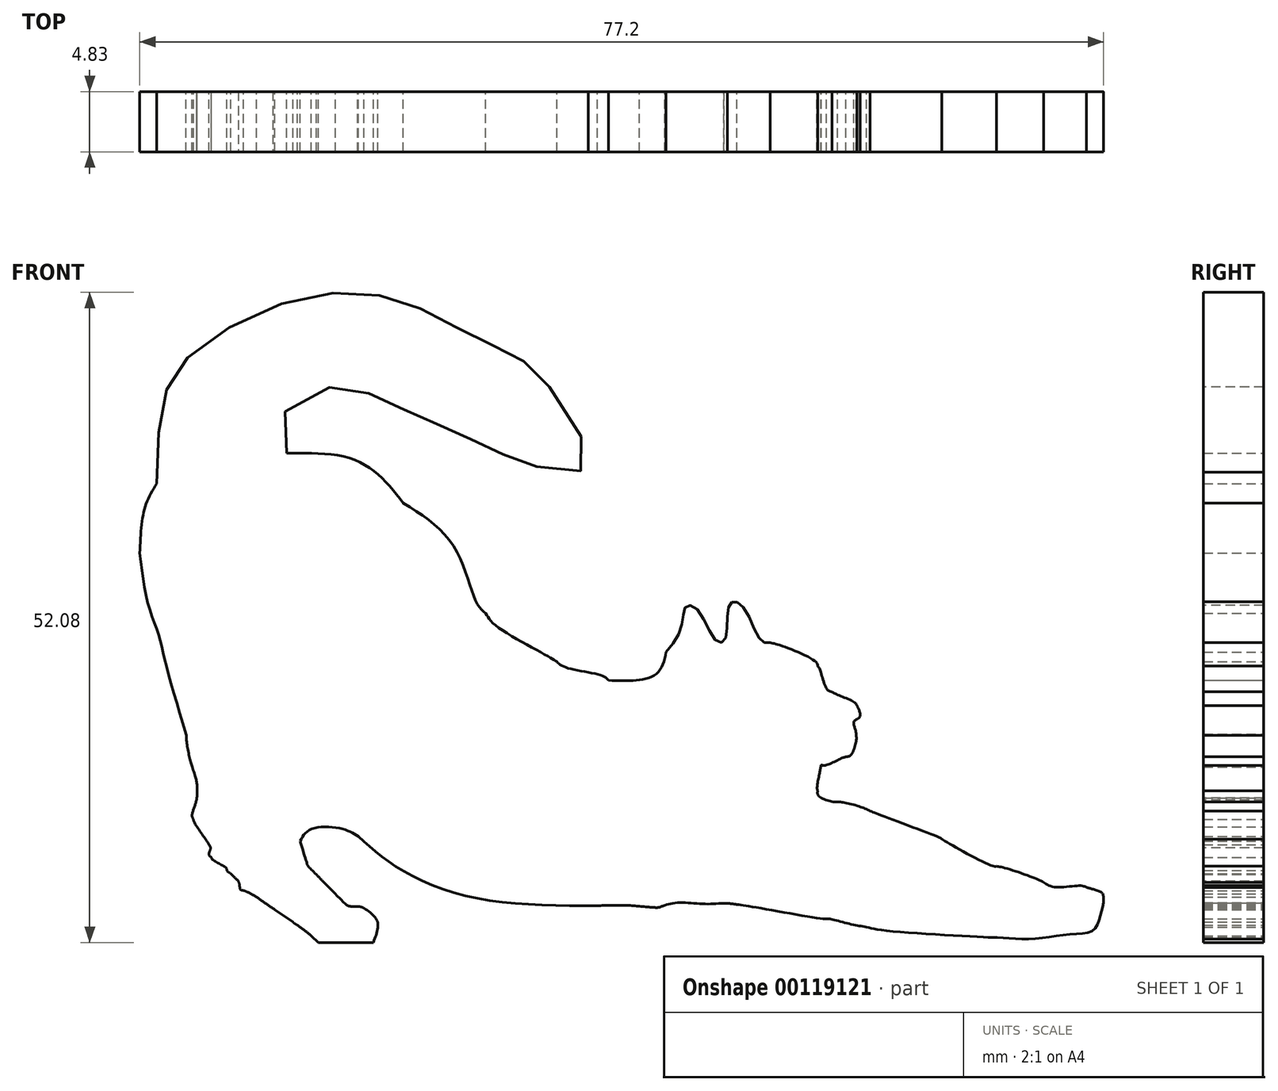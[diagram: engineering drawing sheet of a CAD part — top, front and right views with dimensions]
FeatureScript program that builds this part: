
annotation { "Feature Type Name" : "Feature", "Feature Type Description" : "" }
export const myFeature = defineFeature(function(context is Context, id is Id, definition is map)
    precondition{}
    {
        {
            var Q0;
            Q0=qCreatedBy(makeId("Front.planeOp"),FACE);
            var sketch = newSketch(context, id + "F0", { "sketchPlane" : qUnion([Q0])});
            skFitSpline(sketch, "E0", {"points": [v(-36.48, 1.84) * mm, v(-37.26, 0.43) * mm, v(-37.67, -1.27) * mm, v(-37.84, -3.74) * mm]});
            skFitSpline(sketch, "E1", {"points": [v(-34.12, -18.23) * mm, v(-34.07, -18.96) * mm, v(-33.85, -20.1) * mm, v(-33.63, -20.87) * mm]});
            skFitSpline(sketch, "E2", {"points": [v(-33.63, -20.87) * mm, v(-33.34, -21.84) * mm, v(-33.24, -22.45) * mm, v(-33.27, -23.33) * mm]});
            skFitSpline(sketch, "E3", {"points": [v(-33.27, -23.33) * mm, v(-33.27, -23.33) * mm, v(-33.27, -23.33) * mm, v(-33.27, -23.34) * mm]});
            skFitSpline(sketch, "E4", {"points": [v(-33.27, -23.34) * mm, v(-33.28, -23.4) * mm, v(-33.29, -23.46) * mm, v(-33.3, -23.5) * mm]});
            skFitSpline(sketch, "E5", {"points": [v(-33.3, -23.5) * mm, v(-33.48, -24.1) * mm, v(-33.66, -24.74) * mm, v(-33.54, -25.07) * mm]});
            skFitSpline(sketch, "E6", {"points": [v(-33.54, -25.07) * mm, v(-33.45, -25.34) * mm, v(-32.6, -26.61) * mm, v(-32.29, -27.08) * mm]});
            skFitSpline(sketch, "E7", {"points": [v(-32.29, -27.08) * mm, v(-32.24, -27.17) * mm, v(-32.2, -27.26) * mm, v(-32.15, -27.34) * mm]});
            skFitSpline(sketch, "E8", {"points": [v(-32.15, -27.34) * mm, v(-32.19, -27.46) * mm, v(-32.3, -27.89) * mm, v(-32.12, -28.1) * mm]});
            skFitSpline(sketch, "E9", {"points": [v(-32.12, -28.1) * mm, v(-31.93, -28.35) * mm, v(-30.93, -28.94) * mm, v(-30.86, -29.15) * mm]});
            skFitSpline(sketch, "E10", {"points": [v(-30.86, -29.15) * mm, v(-30.83, -29.23) * mm, v(-30.7, -29.31) * mm, v(-30.55, -29.4) * mm]});
            skFitSpline(sketch, "E11", {"points": [v(-30.55, -29.4) * mm, v(-30.36, -29.6) * mm, v(-30.15, -29.8) * mm, v(-29.95, -30) * mm]});
            skFitSpline(sketch, "E12", {"points": [v(-29.95, -30) * mm, v(-29.85, -30.31) * mm, v(-29.77, -30.68) * mm, v(-29.52, -30.76) * mm]});
            skFitSpline(sketch, "E13", {"points": [v(-29.52, -30.76) * mm, v(-29.39, -30.8) * mm, v(-28.95, -31.02) * mm, v(-28.49, -31.27) * mm]});
            skFitSpline(sketch, "E14", {"points": [v(-28.49, -31.27) * mm, v(-28.11, -31.55) * mm, v(-27.58, -31.92) * mm, v(-27.03, -32.29) * mm]});
            skFitSpline(sketch, "E15", {"points": [v(-25.58, -33.3) * mm, v(-25.47, -33.38) * mm, v(-25.35, -33.46) * mm, v(-25.22, -33.53) * mm]});
            skFitSpline(sketch, "E16", {"points": [v(-25.22, -33.53) * mm, v(-24.75, -33.88) * mm, v(-24.33, -34.2) * mm, v(-24.11, -34.39) * mm]});
            skFitSpline(sketch, "E17", {"points": [v(-19.87, -32.16) * mm, v(-20.06, -32.1) * mm, v(-20.24, -32.05) * mm, v(-20.38, -32.04) * mm]});
            skFitSpline(sketch, "E18", {"points": [v(-20.38, -32.04) * mm, v(-20.95, -32.03) * mm, v(-21.22, -31.94) * mm, v(-22.16, -31.04) * mm]});
            skLineSegment(sketch, "E19", {"start": v(-24.11, -34.39) * mm, "end": v(-23.52, -34.92) * mm});
            skLineSegment(sketch, "E20", {"start": v(-23.52, -34.92) * mm, "end": v(-19.13, -34.92) * mm});
            skFitSpline(sketch, "E21", {"points": [v(-22.89, -30.31) * mm, v(-23.13, -30.06) * mm, v(-23.4, -29.79) * mm, v(-23.7, -29.47) * mm]});
            skFitSpline(sketch, "E22", {"points": [v(-23.7, -29.47) * mm, v(-24.36, -28.8) * mm, v(-24.43, -28.66) * mm, v(-25, -26.8) * mm]});
            skFitSpline(sketch, "E23", {"points": [v(-1.19, -31.98) * mm, v(-0.15, -31.94) * mm, v(1.36, -31.96) * mm, v(2.18, -32.02) * mm]});
            skFitSpline(sketch, "E24", {"points": [v(2.18, -32.02) * mm, v(3.4, -32.12) * mm, v(3.76, -32.1) * mm, v(4.2, -31.93) * mm]});
            skFitSpline(sketch, "E25", {"points": [v(4.2, -31.93) * mm, v(5.35, -31.72) * mm, v(7.25, -31.83) * mm, v(8.93, -31.78) * mm]});
            skFitSpline(sketch, "E26", {"points": [v(8.93, -31.78) * mm, v(8.94, -31.78) * mm, v(8.95, -31.78) * mm, v(8.96, -31.78) * mm]});
            skFitSpline(sketch, "E27", {"points": [v(8.96, -31.78) * mm, v(9.34, -31.8) * mm, v(9.7, -31.83) * mm, v(10, -31.88) * mm]});
            skFitSpline(sketch, "E28", {"points": [v(10, -31.88) * mm, v(11.57, -32.12) * mm, v(16.89, -33.03) * mm, v(17.17, -33.03) * mm]});
            skFitSpline(sketch, "E29", {"points": [v(17.17, -33.03) * mm, v(17.45, -33.04) * mm, v(18.9, -33.4) * mm, v(20.39, -33.69) * mm]});
            skFitSpline(sketch, "E30", {"points": [v(20.39, -33.69) * mm, v(21.88, -33.97) * mm, v(30.2, -34.5) * mm, v(30.85, -34.53) * mm]});
            skFitSpline(sketch, "E31", {"points": [v(39.35, -31.27) * mm, v(39.24, -30.94) * mm, v(38.48, -30.64) * mm, v(38, -30.5) * mm]});
            skFitSpline(sketch, "E32", {"points": [v(38, -30.5) * mm, v(37.52, -30.37) * mm, v(35.45, -30.48) * mm, v(34.57, -30.1) * mm]});
            skFitSpline(sketch, "E33", {"points": [v(34.57, -30.1) * mm, v(33.69, -29.7) * mm, v(31.32, -28.91) * mm, v(30.8, -28.82) * mm]});
            skFitSpline(sketch, "E34", {"points": [v(30.8, -28.82) * mm, v(30.27, -28.72) * mm, v(26.6, -26.76) * mm, v(26.4, -26.64) * mm]});
            skFitSpline(sketch, "E35", {"points": [v(26.4, -26.64) * mm, v(26.2, -26.51) * mm, v(21.63, -24.77) * mm, v(20.67, -24.38) * mm]});
            skFitSpline(sketch, "E36", {"points": [v(20.67, -24.38) * mm, v(19.71, -24) * mm, v(18.39, -23.68) * mm, v(18.06, -23.67) * mm]});
            skFitSpline(sketch, "E37", {"points": [v(18.06, -23.67) * mm, v(17.74, -23.66) * mm, v(16.54, -23.18) * mm, v(16.47, -22.78) * mm]});
            skFitSpline(sketch, "E38", {"points": [v(16.47, -22.78) * mm, v(16.42, -22.51) * mm, v(16.6, -21.46) * mm, v(16.72, -20.74) * mm]});
            skFitSpline(sketch, "E39", {"points": [v(16.72, -20.74) * mm, v(16.73, -20.73) * mm, v(16.76, -20.7) * mm, v(16.76, -20.71) * mm]});
            skFitSpline(sketch, "E40", {"points": [v(16.76, -20.71) * mm, v(17.13, -20.72) * mm, v(18.31, -20.2) * mm, v(18.72, -20.04) * mm]});
            skFitSpline(sketch, "E41", {"points": [v(18.72, -20.04) * mm, v(19.13, -19.9) * mm, v(19.57, -18.69) * mm, v(19.54, -18.32) * mm]});
            skFitSpline(sketch, "E42", {"points": [v(19.54, -18.32) * mm, v(19.5, -17.96) * mm, v(19.36, -17.27) * mm, v(19.61, -17.03) * mm]});
            skFitSpline(sketch, "E43", {"points": [v(19.61, -17.03) * mm, v(19.86, -16.8) * mm, v(19.72, -16.14) * mm, v(19.6, -15.94) * mm]});
            skFitSpline(sketch, "E44", {"points": [v(19.6, -15.94) * mm, v(19.48, -15.73) * mm, v(18, -15.05) * mm, v(17.6, -14.83) * mm]});
            skFitSpline(sketch, "E45", {"points": [v(17.6, -14.83) * mm, v(17.2, -14.62) * mm, v(16.68, -13.15) * mm, v(16.48, -12.78) * mm]});
            skFitSpline(sketch, "E46", {"points": [v(16.48, -12.78) * mm, v(16.3, -12.42) * mm, v(13.55, -11.14) * mm, v(12.67, -10.9) * mm]});
            skFitSpline(sketch, "E47", {"points": [v(-0.3, -13.92) * mm, v(-0.82, -13.54) * mm, v(-3.68, -12.9) * mm, v(-4.43, -12.44) * mm]});
            skFitSpline(sketch, "E48", {"points": [v(-4.43, -12.44) * mm, v(-5.2, -11.97) * mm, v(-9.33, -9.51) * mm, v(-10.12, -8.56) * mm]});
            skFitSpline(sketch, "E49", {"points": [v(-10.12, -8.56) * mm, v(-10.9, -7.61) * mm, v(-12.7, -3.2) * mm, v(-17.45, 0.7) * mm]});
            skFitSpline(sketch, "E50", {"points": [v(-16.5, -0.04) * mm, v(-21.18, 3.92) * mm, v(-27.92, 4.4) * mm, v(-28.67, 5) * mm]});
            skFitSpline(sketch, "E51", {"points": [v(-19.13, -34.92) * mm, v(-18.81, -33.24) * mm, v(-19.87, -32.16) * mm], "startDerivative": vector(1.35, 3.53) * mm, "endDerivative": vector(-2.88, 1.97) * mm});
            skLineSegment(sketch, "E52", {"start": v(-27.03, -32.29) * mm, "end": v(-25.58, -33.3) * mm});
            skLineSegment(sketch, "E53", {"start": v(-22.89, -30.31) * mm, "end": v(-22.16, -31.04) * mm});
            skPoint(sketch, "E54", {"position": v(-24.12, -25.84) * mm});
            skPoint(sketch, "E55", {"position": v(-21.6, -25.82) * mm});
            skFitSpline(sketch, "E56", {"points": [v(-25, -26.8) * mm, v(-24.12, -25.84) * mm, v(-21.6, -25.82) * mm, v(-20.34, -26.42) * mm], "startDerivative": vector(2.15, 3.92) * mm, "endDerivative": vector(3.45, -2.24) * mm});
            skPoint(sketch, "E57", {"position": v(-17.5, -28.72) * mm});
            skPoint(sketch, "E58", {"position": v(-11.33, -31.28) * mm});
            skFitSpline(sketch, "E59", {"points": [v(-20.34, -26.42) * mm, v(-17.5, -28.72) * mm, v(-11.33, -31.28) * mm, v(-1.19, -31.98) * mm], "startDerivative": vector(10.16, -9.32) * mm, "endDerivative": vector(25.66, -0.09) * mm});
            skPoint(sketch, "E60", {"position": v(33.44, -34.64) * mm});
            skPoint(sketch, "E61", {"position": v(36.63, -34.28) * mm});
            skFitSpline(sketch, "E62", {"points": [v(30.85, -34.53) * mm, v(33.44, -34.64) * mm, v(36.63, -34.28) * mm, v(38.55, -33.94) * mm, v(39.12, -32.72) * mm, v(39.35, -31.27) * mm], "startDerivative": vector(10.58, -0.3) * mm, "endDerivative": vector(-0.7, 11.3) * mm});
            skPoint(sketch, "E63", {"position": v(4.31, -11.66) * mm});
            skFitSpline(sketch, "E64", {"points": [v(-37.84, -3.74) * mm, v(-37.2, -7.7) * mm, v(-36.33, -10.3) * mm, v(-35.74, -12.65) * mm, v(-34.12, -18.23) * mm], "startDerivative": vector(1.84, -15.9) * mm, "endDerivative": vector(5.96, -19.6) * mm});
            skPoint(sketch, "E65", {"position": v(-35.98, 8.38) * mm});
            skPoint(sketch, "E66", {"position": v(-34.02, 11.9) * mm});
            skPoint(sketch, "E67", {"position": v(-27.06, 16.03) * mm});
            skPoint(sketch, "E68", {"position": v(-20.06, 17.12) * mm});
            skPoint(sketch, "E69", {"position": v(-15.1, 15.73) * mm});
            skPoint(sketch, "E70", {"position": v(-10.98, 13.58) * mm});
            skPoint(sketch, "E71", {"position": v(-5, 9.54) * mm});
            skPoint(sketch, "E72", {"position": v(-2.05, 3.22) * mm});
            skPoint(sketch, "E73", {"position": v(-6.48, 3.33) * mm});
            skPoint(sketch, "E74", {"position": v(-9.42, 4.48) * mm});
            skPoint(sketch, "E75", {"position": v(-13, 6.17) * mm});
            skPoint(sketch, "E76", {"position": v(-16.16, 7.54) * mm});
            skPoint(sketch, "E77", {"position": v(-19.95, 9.22) * mm});
            skPoint(sketch, "E78", {"position": v(-24.69, 8.8) * mm});
            skFitSpline(sketch, "E79", {"points": [v(-36.48, 1.84) * mm, v(-35.98, 8.38) * mm, v(-34.02, 11.9) * mm, v(-27.06, 16.03) * mm, v(-20.06, 17.12) * mm, v(-15.1, 15.73) * mm, v(-10.98, 13.58) * mm, v(-7.55, 11.9) * mm, v(-5, 9.54) * mm, v(-2.05, 3.22) * mm, v(-6.48, 3.33) * mm, v(-9.42, 4.48) * mm, v(-13, 6.17) * mm, v(-16.16, 7.54) * mm, v(-19.95, 9.22) * mm, v(-24.69, 8.8) * mm, v(-26.06, 4.27) * mm], "startDerivative": vector(0.2, 93.83) * mm, "endDerivative": vector(119.05, -59.42) * mm});
            skPoint(sketch, "E80", {"position": v(10.43, -10.5) * mm});
            skPoint(sketch, "E81", {"position": v(5.58, -9.5) * mm});
            skPoint(sketch, "E82", {"position": v(5.9, -8.02) * mm});
            skPoint(sketch, "E83", {"position": v(6.82, -8.26) * mm});
            skPoint(sketch, "E84", {"position": v(9.25, -8.34) * mm});
            skPoint(sketch, "E85", {"position": v(9.7, -7.62) * mm});
            skPoint(sketch, "E86", {"position": v(10.65, -8.26) * mm});
            skFitSpline(sketch, "E87", {"points": [v(4.31, -11.66) * mm, v(5.58, -9.5) * mm, v(5.9, -8.02) * mm, v(6.82, -8.26) * mm, v(8.36, -10.78) * mm, v(9.04, -10.64) * mm, v(9.25, -8.34) * mm, v(9.7, -7.62) * mm, v(10.65, -8.26) * mm, v(11.92, -10.72) * mm, v(12.67, -10.9) * mm], "startDerivative": vector(13.35, 16.23) * mm, "endDerivative": vector(11, 0.76) * mm});
            skPoint(sketch, "E88", {"position": v(2.06, -13.9) * mm});
            skPoint(sketch, "E89", {"position": v(3.65, -13.29) * mm});
            skFitSpline(sketch, "E90", {"points": [v(-0.3, -13.92) * mm, v(2.06, -13.9) * mm, v(3.65, -13.29) * mm, v(4.31, -11.66) * mm], "startDerivative": vector(6.53, -0.26) * mm, "endDerivative": vector(1.1, 5.87) * mm});
            skSolve(sketch);
        }
        {
            var Q0;
            Q0=makeQuery(id+"F0.imprint","IMPRINT",FACE,{"disambiguationData":[TD([[makeQuery(id+"F0.imprint","IMPRINT",EDGE,{"derivedFrom":sQuery(id+"F0.wireOp",EDGE,"E0")}),1.0]])]});
            extrude(context, id + "F1", {"entities" : qUnion([Q0]), "depth" : 4.83 * mm});
        }
    });
